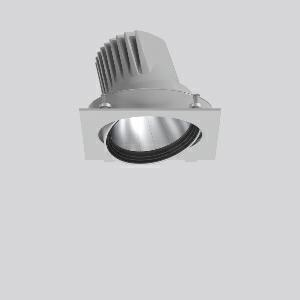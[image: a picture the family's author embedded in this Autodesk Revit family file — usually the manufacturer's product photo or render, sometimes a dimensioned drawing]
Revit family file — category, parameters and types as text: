
# Revit family: magcardo_maxi_722207_004_76_e9b0
name_source: partatom
category: Lighting Fixtures
units: mm (PartAtom-declared; Revit-internal decimal feet)

## family parameters
Cut with Voids When Loaded = No
Host = Face
Light Source = No
Part Type = Normal
Room Calculation Point = No
Round Connector Dimension = Use Diameter
Shared = No

## types (1)
- MAGCARDO maxi (1 x LED Modul 920 meat+, 2200 lm, 2000)
    Apparent Load = 33 VA
    Approval mark = CE
    CIE Flux Codes = 100 100 100 100 100
    Color Rendering = 90
    Color Temperature = 2000
    Default Elevation = 1800 mm
    Description = Series: MAGCARDO maxi
Projector unit for tool-free mounting in separate recessed frame. Luminaire top: die-cast aluminium, powder-coated. Rotation range 356° and swivel range ± 35°. Inner cover prevents view into the false ceiling. Black plastic ring and recessed LED to prevent glare from the side. Optical assembly with reflector made of MIRO-Silver with 98% total light reflection for outstanding efficiency - can be changed without tools. Special LED for illumination of meat included. Magnetic click locking mechanism for quick and convenient installation without tools: insert the recessed frame (1, 2 or 3-lamp) with clamp fastener (no tools required), push the luminaire head with the base plate into the recessed frame and fix magnetically. Including separate LED converter with connecting cable 600 mm.High quality converter without flickering and stroboscopic effect. Through-wiring box (5 pole) available as accessory. The following accessories can be mounted without use of tools: interchangeable lenses, honeycomb louvre, clear and frosted diffusers, white interchangeable plastic ring.Modular design: recessed mounting frame must be ordered separately! 
Colour: silver
Length: 172 mm
Width: 167 mm
Height: 137 mm
Recess height: 155 mm
Lamp: LED
Socket: without socket
Colour temperature: meat +
System power: 33 W
Rated luminous flux: 2200 lm
Luminous efficiency: 67 lm/W
Control gear: Converter, dimmable, DALI
Protection class: II
Type of protection: IP 20
    Height = 0 mm  [stored 0 ft]
    Lamp = 1 x LED Modul 920 meat+
    Lamp Light Flux = 2200 lm
    Lamp count = 1
    Length = 172 mm
    Lifetime = 50000 h
    Luminous efficacy = 67 lm/W
    Manufacturer = RZB
    ModVariant = No
    Model = 722207.004.76
    Mounting Place = Ceiling, Wall
    Mounting Type = Recessed
    Number of Poles = 1
    OnlyDefault = Yes
    Power Factor = 1
    Product Name = MAGCARDO maxi
    Product group = Recessed projectors
    ProductGroupID = 401
    Protection Class = Protection class II
    Protection Degree = IP 20
    RLX_Detail_Level = 1
    RLX_Emergency_Light_Flux = 0 lm
    RLX_Emergency_Type = 0
    RLX_Emergency_Type_DB = No
    RlxData = <blob elided: 40901 chars, md5=2c5deb2f>
    Socket = socket
    Standby Power = 0 W
    System Light Flux = 2200 lm
    System Power = 33 W
    Type Comments = Product without accessories
    Type Image = 722045.004.jpg
    URL = http://relux.com
    VarID = ---
    Voltage = 230 V
    Voltage Range = 220-240 V
    Weight = 0.00 kg
    Width = 167 mm

note: [stored X ft] marks values corroborated as IEEE doubles in the binary element streams (Revit-internal decimal feet)

## geometry (parser evidence)
native form markers: Blend x4, Sweep x11
no freeform markers — native parametric forms only
